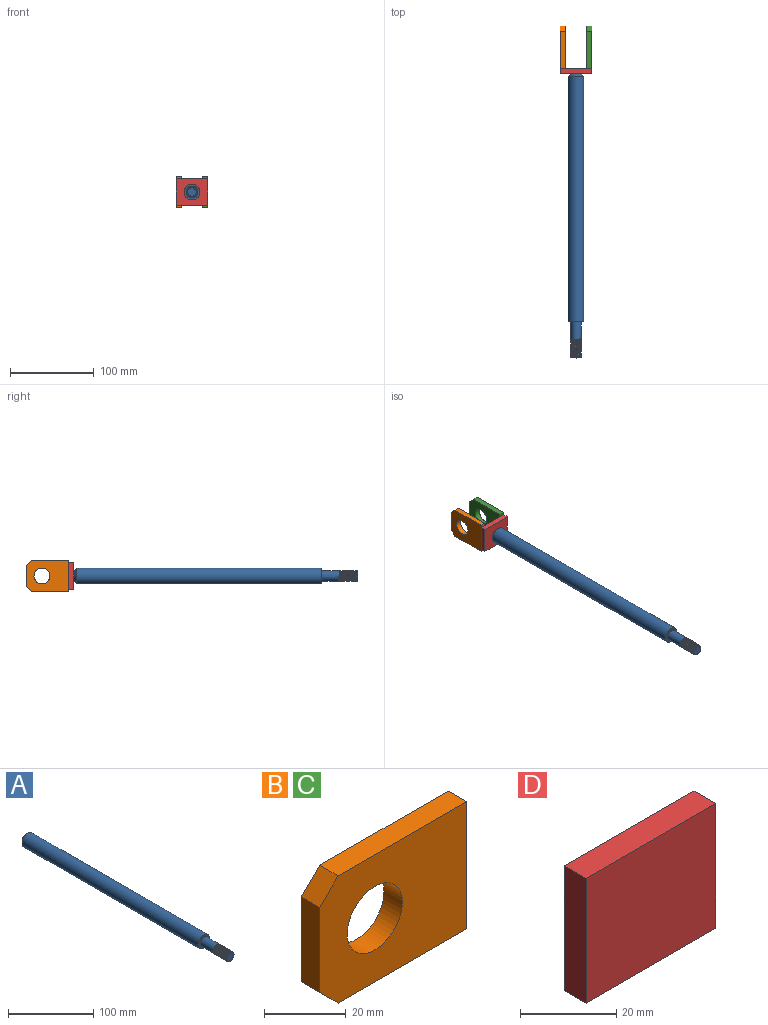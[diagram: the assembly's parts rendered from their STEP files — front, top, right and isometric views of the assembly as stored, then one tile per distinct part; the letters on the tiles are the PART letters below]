
ASSEMBLY  parts=4 mates=3
PART A: 22 faces, bbox 19.9x341.6x19.9 mm
  f0: cylinder r=6.35mm len=12.7mm, axis (0,1,0), area 17.1mm2, adj f1,f12,f15,f16
  f1: cylinder r=6.35mm len=12.7mm, axis (0,1,0), area 17.1mm2, adj f0,f2,f15,f16
  f2: cylinder r=6.35mm len=12.7mm, axis (0,1,0), area 17.2mm2, adj f1,f3,f15,f16
  f3: cylinder r=6.35mm len=12.7mm, axis (0,1,0), area 17.2mm2, adj f2,f4,f15,f16
  f4: cylinder r=6.35mm len=12.7mm, axis (0,1,0), area 17.1mm2, adj f3,f5,f15,f16
  f5: cylinder r=6.35mm len=12.7mm, axis (0,1,0), area 17.2mm2, adj f4,f6,f15,f16
  f6: cylinder r=6.35mm len=12.7mm, axis (0,1,0), area 17.2mm2, adj f5,f7,f15,f16
  f7: cylinder r=6.35mm len=12.7mm, axis (0,1,0), area 17.1mm2, adj f6,f8,f15,f16
  f8: cylinder r=6.35mm len=12.7mm, axis (0,1,0), area 17.1mm2, adj f7,f9,f15,f16
  f9: cylinder r=6.35mm len=12.7mm, axis (0,1,0), area 17.2mm2, adj f8,f10,f15,f16
  f10: cylinder r=6.35mm len=12.7mm, axis (0,1,0), area 17.2mm2, adj f9,f11,f15,f16
  f11: cylinder r=6.35mm len=12.61mm, axis (0,1,0), area 6.2mm2, adj f10,f13,f15,f16
  f12: cylinder r=6.35mm len=21.29mm, axis (0,1,0), area 810.5mm2, adj f0,f14,f15,f21
  f13: plane 12.64x12.64mm, normal (0,-1,0), area 107.6mm2, adj f11,f15,f16
  f14: plane 1.52x1.32mm, normal (0,0,-1), area 1mm2, adj f12,f15,f16
  f15: bspline ~24.86x14.66mm, area 658.3mm2, adj f0,f1,f2,f3,f4,f5,f6,f7
  f16: bspline ~24.21x14.66mm, area 636mm2, adj f0,f1,f2,f3,f4,f5,f6,f7
  f17: cylinder r=9.53mm len=292.38mm, axis (0,1,0), area 17498.1mm2, adj f18,f20
  f18: plane 19.05x19.05mm, normal (0,-1,0), area 126.1mm2, adj f17,f21
  f19: plane 12.45x12.45mm, normal (0,1,0), area 121.7mm2, adj f20
  f20: cone r=9.53mm half-angle=45deg, axis (0,-1,0), area 231mm2, adj f17,f19
  f21: torus R=7.11mm, axis (0,-1,0), area 49.8mm2, adj f12,f18
PART B: 9 faces, bbox 50.8x6.4x38.1 mm
  f0: plane 25.4x6.35mm, normal (-1,0,0), area 161.3mm2, adj f1,f6,f7,f8
  f1: plane 6.35x6.35mm, normal (-0.71,0,-0.71), area 57mm2, adj f0,f2,f7,f8
  f2: plane 44.45x6.35mm, normal (0,0,-1), area 282.3mm2, adj f1,f3,f7,f8
  f3: plane 38.1x6.35mm, normal (1,0,0), area 241.9mm2, adj f2,f4,f7,f8
  f4: plane 44.45x6.35mm, normal (0,0,1), area 282.3mm2, adj f3,f6,f7,f8
  f5: cylinder r=9.53mm len=19.05mm, axis (0,1,0), area 380mm2, adj f7,f8
  f6: plane 6.35x6.35mm, normal (-0.71,0,0.71), area 57mm2, adj f0,f4,f7,f8
  f7: plane 50.8x38.1mm, normal (0,-1,0), area 1610.1mm2, adj f0,f1,f2,f3,f4,f5,f6
  f8: plane 50.8x38.1mm, normal (0,1,0), area 1610.1mm2, adj f0,f1,f2,f3,f4,f5,f6
PART C: same geometry as B
PART D: 6 faces, bbox 38.1x6.4x31.8 mm
  f0: plane 31.75x6.35mm, normal (-1,0,0), area 201.6mm2, adj f1,f3,f4,f5
  f1: plane 38.1x6.35mm, normal (0,0,-1), area 241.9mm2, adj f0,f2,f4,f5
  f2: plane 31.75x6.35mm, normal (1,0,0), area 201.6mm2, adj f1,f3,f4,f5
  f3: plane 38.1x6.35mm, normal (0,0,1), area 241.9mm2, adj f0,f2,f4,f5
  f4: plane 38.1x31.75mm, normal (0,-1,0), area 1209.7mm2, adj f0,f1,f2,f3
  f5: plane 38.1x31.75mm, normal (0,1,0), area 1209.7mm2, adj f0,f1,f2,f3
PLACE A at identity
PLACE B rot(axis=(0.71,-0.71,0),180deg) t=(-15.87,179.59,0)mm
PLACE C rot(axis=(0.71,-0.71,0),180deg) t=(15.88,179.59,0)mm
PLACE D rot(axis=(1,0,0),180deg) t=(0,151.02,0)mm
MATE fastened C.f3 <-> D.f4  axis (0,-1,0) through (15.88,154.19,0)mm
MATE fastened B.f3 <-> D.f4  axis (0,-1,0) through (-15.87,154.19,0)mm
MATE fastened D.f5 <-> A.f17  axis (0,-1,0) through (0,147.84,0)mm
